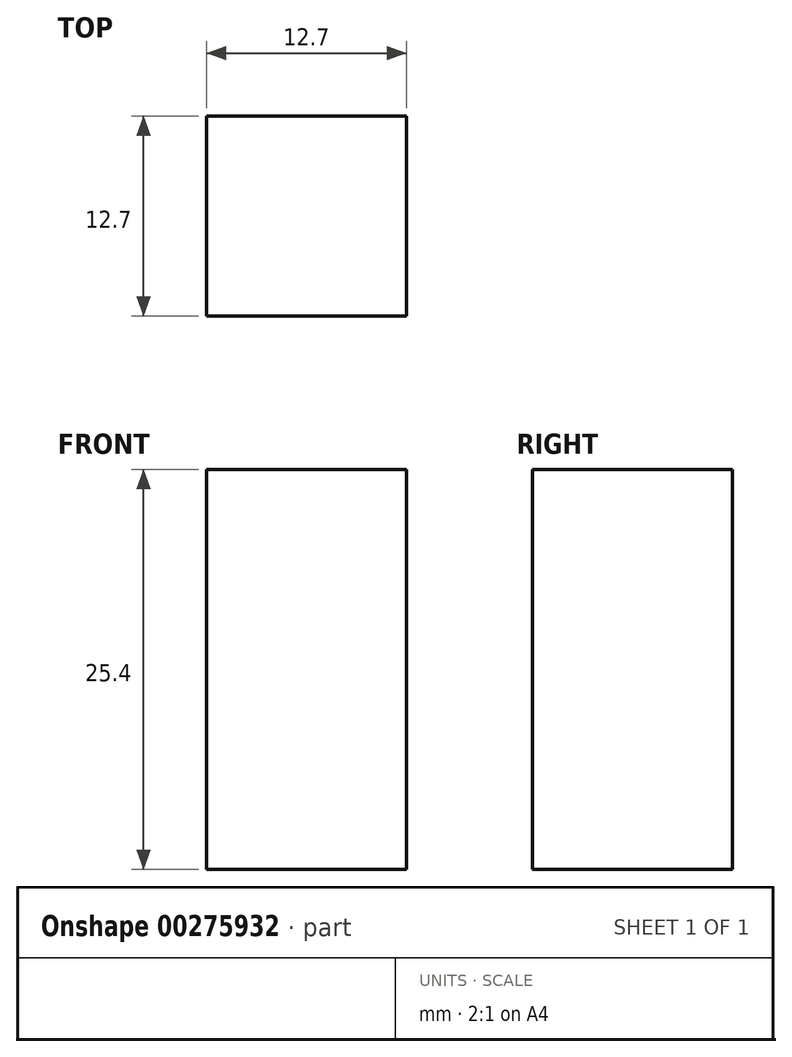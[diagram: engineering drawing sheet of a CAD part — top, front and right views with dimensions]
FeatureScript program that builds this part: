
annotation { "Feature Type Name" : "Feature", "Feature Type Description" : "" }
export const myFeature = defineFeature(function(context is Context, id is Id, definition is map)
    precondition{}
    {
        {
            var Q0;
            Q0=qCreatedBy(makeId("Top.planeOp"),FACE);
            var sketch = newSketch(context, id + "F0", { "sketchPlane" : qUnion([Q0])});
            skLineSegment(sketch, "E0.bottom", {"start": v(6.35, 5.25) * mm, "end": v(-6.35, 5.25) * mm});
            skLineSegment(sketch, "E0.top", {"start": v(6.35, -7.45) * mm, "end": v(-6.35, -7.45) * mm});
            skLineSegment(sketch, "E0.left", {"start": v(6.35, 5.25) * mm, "end": v(6.35, -7.45) * mm});
            skLineSegment(sketch, "E0.right", {"start": v(-6.35, 5.25) * mm, "end": v(-6.35, -7.45) * mm});
            skPoint(sketch, "E0.middle", {"position": v(0, -1.1) * mm});
            skSolve(sketch);
        }
        {
            var Q0;
            Q0=qSketchRegion(id+"F0",true);
            extrude(context, id + "F1", {"entities" : qUnion([Q0]), "depth" : 25.4 * mm});
        }
    });
